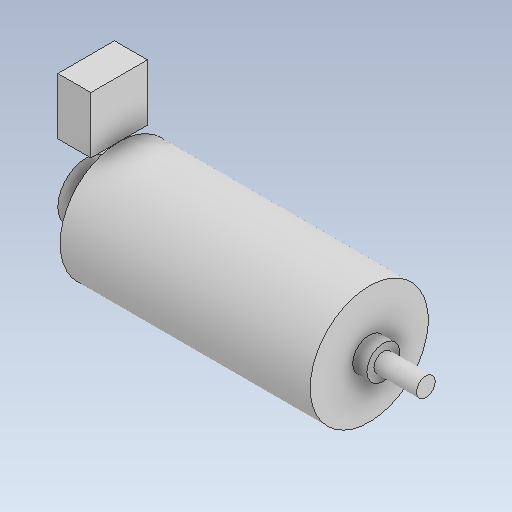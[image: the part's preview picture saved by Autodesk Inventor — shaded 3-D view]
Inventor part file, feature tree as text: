
AUTODESK INVENTOR PART (.ipt)
format: ipt  version: 2021 (Build 250183000, 183)  size: 129,024 bytes
history: native  units: mm
features: other x2, revolve x1, plane x1, extrude x1, sketch x1
ambient origin geometry x8: Origin, YZ Plane, XZ Plane, XY Plane, X Axis, Y Axis, Z Axis, Center Point
bodies: Body1 (feature_tree)
feature tree (6):
  other  "00_Mastersketch.ipt"
  revolve  "Umdrehung2"
  plane  "Arbeitsebene1"
  extrude  "Extrusion1"  TaperAngle=90.0deg  [1 undecoded]
  other  "02_motorSketch"
  sketch  "Skizze2"  dims[d0=10.0mm d2=90.0deg d3=12.0mm d4=0.0mm]
note: 1 required parameter value undecoded (feature->parameter linkage not recoverable at this tier; creation-order binding heuristic only, values carry confidence <= 0.55)
